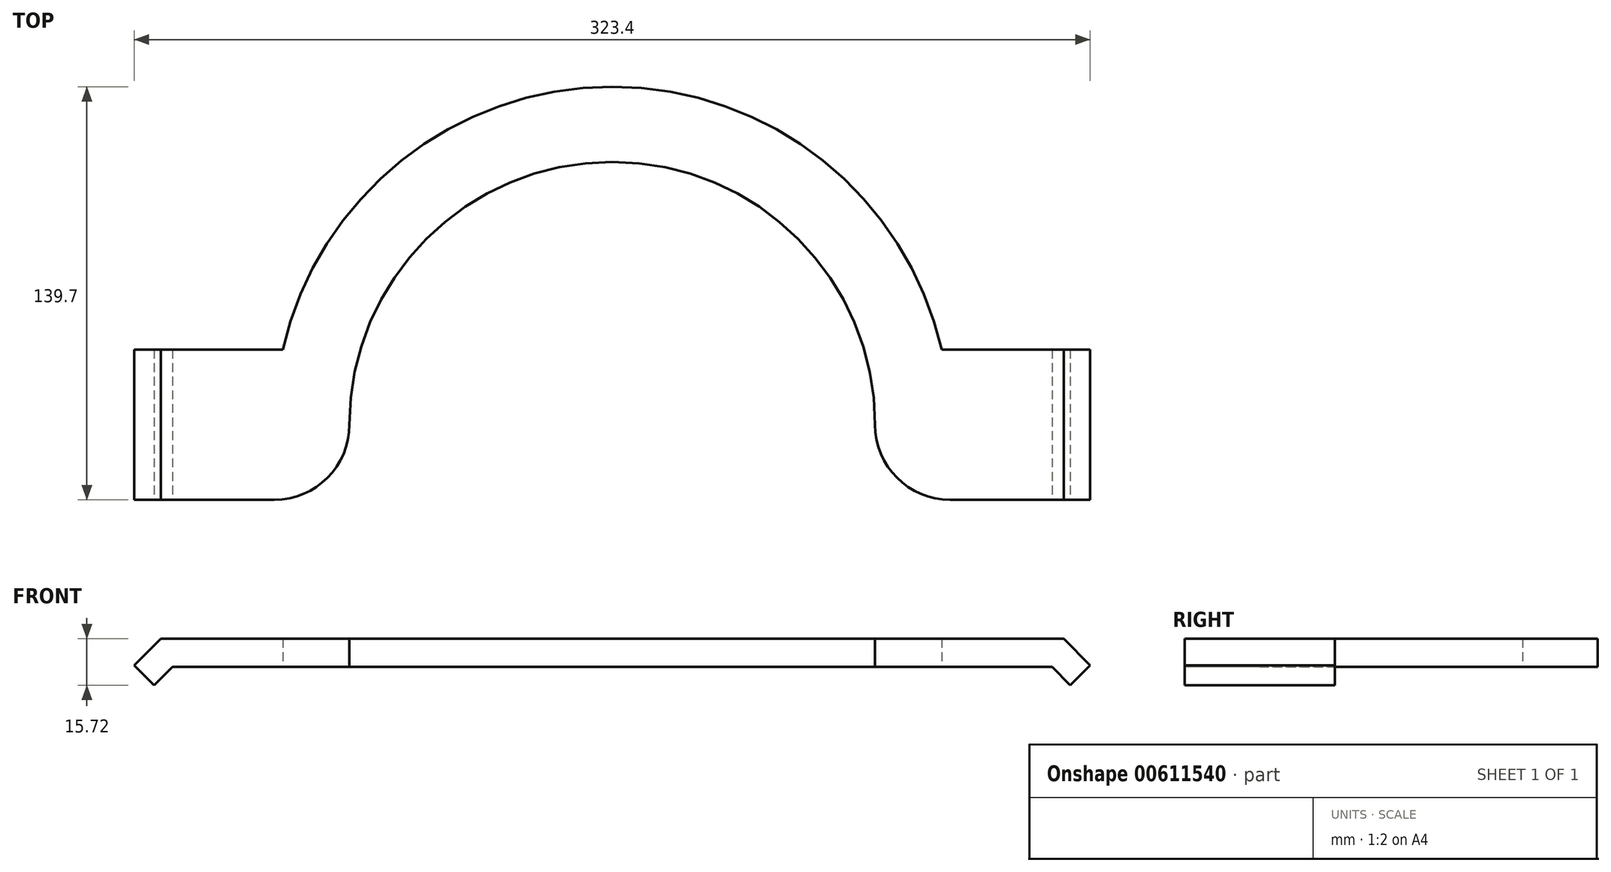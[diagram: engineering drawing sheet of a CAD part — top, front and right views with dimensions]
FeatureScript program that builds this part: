
annotation { "Feature Type Name" : "Feature", "Feature Type Description" : "" }
export const myFeature = defineFeature(function(context is Context, id is Id, definition is map)
    precondition{}
    {
        {
            var Q0;
            Q0=qCreatedBy(makeId("Top.planeOp"),FACE);
            var sketch = newSketch(context, id + "F0", { "sketchPlane" : qUnion([Q0])});
            skArc(sketch, "E0", {"start": v(88.9, 0) * mm, "mid": v(0, 88.9) * mm, "end": v(-88.9, 0) * mm});
            skArc(sketch, "E1", {"start": v(111.44, 25.4) * mm, "mid": v(0, 114.3) * mm, "end": v(-111.44, 25.4) * mm});
            skLineSegment(sketch, "E2.bottom", {"start": v(111.44, 25.4) * mm, "end": v(152.72, 25.4) * mm});
            skLineSegment(sketch, "E2.right", {"start": v(152.72, 25.4) * mm, "end": v(152.72, -25.4) * mm});
            skLineSegment(sketch, "E3.bottom", {"start": v(-111.44, 25.4) * mm, "end": v(-152.72, 25.4) * mm});
            skLineSegment(sketch, "E3.right", {"start": v(-152.72, 25.4) * mm, "end": v(-152.72, -25.4) * mm});
            skLineSegment(sketch, "E4", {"start": v(-88.9, 0) * mm, "end": v(-88.9, 0) * mm});
            skLineSegment(sketch, "E5", {"start": v(88.9, 0) * mm, "end": v(88.9, 0) * mm});
            skLineSegment(sketch, "E6", {"start": v(-152.72, -25.4) * mm, "end": v(-114.3, -25.4) * mm});
            skLineSegment(sketch, "E7", {"start": v(114.3, -25.4) * mm, "end": v(152.72, -25.4) * mm});
            skPoint(sketch, "E8.visualSharp", {"position": v(-88.9, -25.4) * mm});
            skArc(sketch, "E8.filletArc", {"start": v(-114.3, -25.4) * mm, "mid": v(-96.34, -17.96) * mm, "end": v(-88.9, 0) * mm});
            skPoint(sketch, "E9.visualSharp", {"position": v(88.9, -25.4) * mm});
            skArc(sketch, "E9.filletArc", {"start": v(88.9, 0) * mm, "mid": v(96.34, -17.96) * mm, "end": v(114.3, -25.4) * mm});
            skSolve(sketch);
        }
        {
            var Q0;
            Q0 = qSketchRegion(id + "F0", true);
            extrude(context, id + "F1", {"entities" : qUnion([Q0]), "depth" : 9.52 * mm, "offsetDistance" : 25.4 * mm});
        }
        {
            var Q0;
            Q0=makeQuery(id+"F1.opExtrude","SWEPT_FACE",FACE,{"disambiguationData":[OSD([sQuery(id+"F0.wireOp",EDGE,"E7")])]});
            var sketch = newSketch(context, id + "F2", { "sketchPlane" : qUnion([Q0])});
            skLineSegment(sketch, "E10", {"start": v(152.72, 9.53) * mm, "end": v(161.7, 0.54) * mm});
            skLineSegment(sketch, "E11", {"start": v(161.7, 0.54) * mm, "end": v(154.96, -6.2) * mm});
            skLineSegment(sketch, "E12", {"start": v(154.96, -6.2) * mm, "end": v(148.77, 0) * mm});
            skLineSegment(sketch, "E13", {"start": v(148.77, 0) * mm, "end": v(152.72, 9.52) * mm});
            skSolve(sketch);
        }
        {
            var Q0;
            Q0 = qSketchRegion(id + "F2", true);
            var Q1;
            Q1=makeQuery(id+"F1.opExtrude","SWEPT_FACE",FACE,{"disambiguationData":[OSD([sQuery(id+"F0.wireOp",EDGE,"E2.bottom")])]});
            extrude(context, id + "F3", {"entities" : qUnion([Q0]), "operationType" : NewBodyOperationType.ADD, "endBound" : BoundingType.UP_TO_SURFACE, "oppositeDirection" : true, "depth" : 25.4 * mm, "endBoundEntityFace" : qUnion([Q1]), "offsetDistance" : 25.4 * mm});
        }
        {
            var Q0;
            Q0=makeQuery(id+"F1.opExtrude","SWEPT_FACE",FACE,{"disambiguationData":[OSD([sQuery(id+"F0.wireOp",EDGE,"E6")])]});
            var sketch = newSketch(context, id + "F4", { "sketchPlane" : qUnion([Q0])});
            skLineSegment(sketch, "E14", {"start": v(-152.72, 9.52) * mm, "end": v(-161.7, 0.54) * mm});
            skLineSegment(sketch, "E15", {"start": v(-161.7, 0.54) * mm, "end": v(-154.96, -6.2) * mm});
            skLineSegment(sketch, "E16", {"start": v(-154.96, -6.2) * mm, "end": v(-148.77, 0) * mm});
            skLineSegment(sketch, "E17", {"start": v(-148.77, 0) * mm, "end": v(-152.72, 9.53) * mm});
            skSolve(sketch);
        }
        {
            var Q0;
            Q0 = qSketchRegion(id + "F4", true);
            var Q1;
            Q1=makeQuery(id+"F1.opExtrude","SWEPT_FACE",FACE,{"disambiguationData":[OSD([sQuery(id+"F0.wireOp",EDGE,"E3.bottom")])]});
            extrude(context, id + "F5", {"entities" : qUnion([Q0]), "operationType" : NewBodyOperationType.ADD, "endBound" : BoundingType.UP_TO_SURFACE, "oppositeDirection" : true, "depth" : 25.4 * mm, "endBoundEntityFace" : qUnion([Q1]), "offsetDistance" : 25.4 * mm});
        }
    });
